# Revit family: Haworth_JiveTable_FlipBaseLegs
name_source: partatom
category: Furniture Systems
revit_build: Autodesk Revit 2018 (Build: 20170223_1515(x64)
units: mm (PartAtom-declared; Revit-internal decimal feet)

## family parameters
Always vertical = Yes
Cut with Voids When Loaded = No
OmniClass Number = 23.40.70.14.64.21
OmniClass Title = Systems Furniture
Part Type = Normal
Room Calculation Point = No
Round Connector Dimension = Use Diameter
Shared = No
Work Plane-Based = No

## types (4) — shared parameters
Actual Depth = 30"
Actual Height = 29"
Actual Width = 60"
Assembly Code = E2020200
Casters = Yes
Custom Size = No
Depth = 30"
Glides = No
Height = 29"
Leg Finish = Haworth _ Paint _ Graphite
Leg Height = 27 13/16"
Leg Length = 14 141/256"
Manufacturer = Haworth, Inc.
Max. Depth = 60"
Max. Height = 42"
Max. Width = 84"
Min. Depth = 18"
Min. Height = 16"
Min. Width = 24"
Model = Hawoth Jive
Post Leg Spacing = 21 127/128"
Revision Number = 0
Size = Verify Final Dim. w/ Haworth
Standard Depths = 18, 24, 30, 36, 42, 48, 54, 60 in.
Standard Height = 16, 20, 29, 36, 42 in.
Standard Widths = 24, 30, 36, 42, 48, 54, 60, 66, 72, 84 in.
Table Edge Finish = Haworth _ Laminate _ Putty H-AA
Table Finish = Haworth _ Laminate _ Putty H-AA
Table Thickness = 1 3/16"
URL = http://www.haworth.com
URL - Product = http://www.haworth.com
Warranty = http://www.haworth.com
Width = 60"

## per-type parameters (varying)
| type | C Leg Extruded | C Leg Round | Description | Leg Distance | Leg Spacing | T Leg Extruded | T Leg Round |
| 30d 60w 29h - C Leg Extruded - With Casters | Yes | No | Haworth Jive Table Rectangle Legs - 30d 60w 29h - C Leg Extruded - With Casters | 7 91/128" | 7 37/128" | No | No |
| 30d 60w 29h - C Leg Round - With Casters | No | Yes | Haworth Jive Table Rectangle Legs - 30d 60w 29h - C Leg Round - With Casters | 8 53/64" | 6 11/64" | No | No |
| 30d 60w 29h - T Leg Extruded - With Casters | No | No | Haworth Jive Table Rectangle Legs - 30d 60w 29h - T Leg Extruded - With Casters | 7 91/128" | 7 37/128" | Yes | No |
| 30d 60w 29h - T Leg Round - With Casters | No | No | Haworth Jive Table Rectangle Legs - 30d 60w 29h - T Leg Round - With Casters | 8 53/64" | 6 11/64" | No | Yes |

## geometry (parser evidence)
native form markers: Sweep x32
no freeform markers — native parametric forms only
